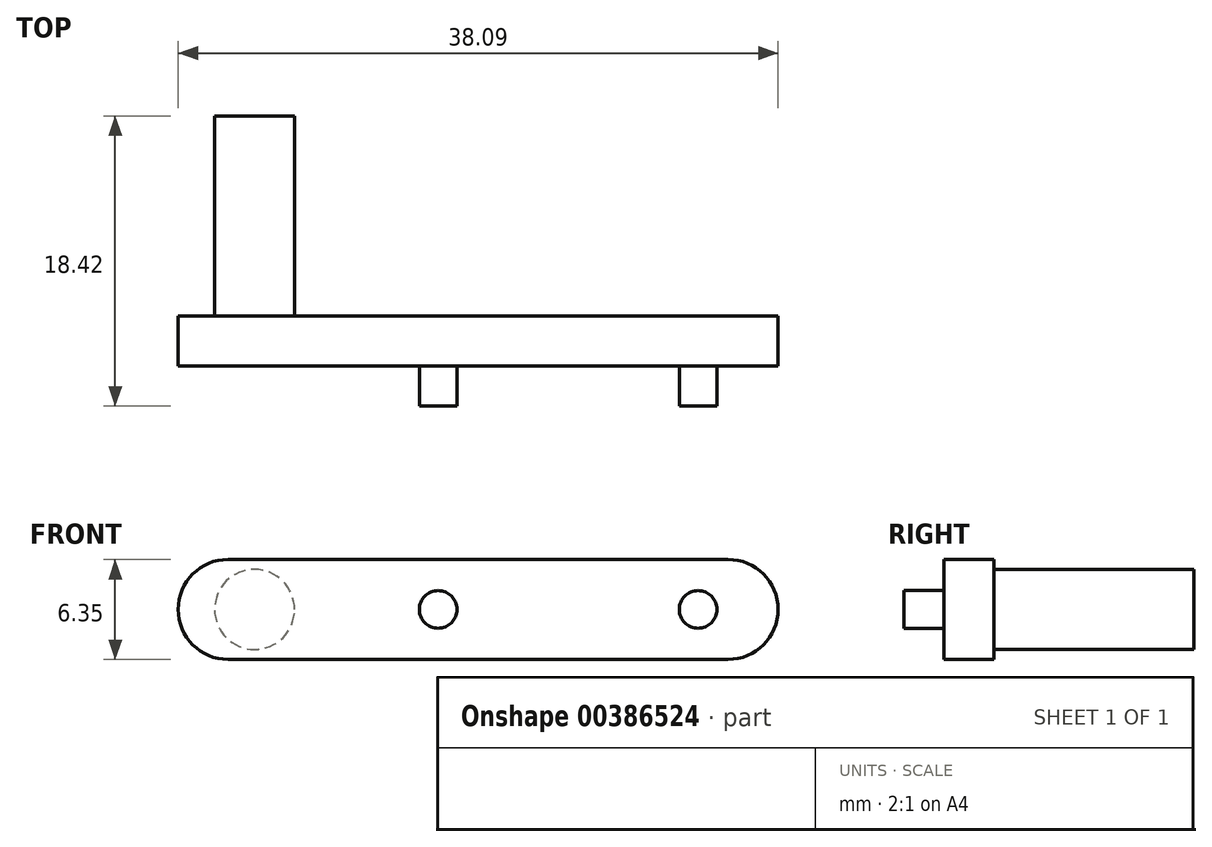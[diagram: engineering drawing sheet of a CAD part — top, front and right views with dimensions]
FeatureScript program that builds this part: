
annotation { "Feature Type Name" : "Feature", "Feature Type Description" : "" }
export const myFeature = defineFeature(function(context is Context, id is Id, definition is map)
    precondition{}
    {
        {
            var Q0;
            Q0=qCreatedBy(makeId("Front.planeOp"),FACE);
            var sketch = newSketch(context, id + "F0", { "sketchPlane" : qUnion([Q0])});
            skArc(sketch, "E0", {"start": v(0, 3.18) * mm, "mid": v(-3.18, 0) * mm, "end": v(0, -3.18) * mm});
            skArc(sketch, "E1", {"start": v(31.75, -3.18) * mm, "mid": v(34.93, 0) * mm, "end": v(31.75, 3.17) * mm});
            skLineSegment(sketch, "E2", {"start": v(0, 3.18) * mm, "end": v(31.75, 3.18) * mm});
            skLineSegment(sketch, "E3", {"start": v(0, -3.17) * mm, "end": v(31.75, -3.18) * mm});
            skSolve(sketch);
        }
        {
            var Q0;
            Q0 = qSketchRegion(id + "F0", true);
            extrude(context, id + "F1", {"entities" : qUnion([Q0]), "depth" : 3.17 * mm});
        }
        {
            var Q0;
            Q0=makeQuery(id+"F1.opExtrude","CAP_FACE",FACE,{"disambiguationData":[OSD([sQuery(id+"F0.wireOp",EDGE,"E0"),sQuery(id+"F0.wireOp",EDGE,"E1"),sQuery(id+"F0.wireOp",EDGE,"E2"),sQuery(id+"F0.wireOp",EDGE,"E3")])],"isStart":false});
            var sketch = newSketch(context, id + "F2", { "sketchPlane" : qUnion([Q0])});
            skCircle(sketch, "E4", {"center": v(13.34, 0) * mm, "radius": 1.2 * mm});
            skSolve(sketch);
        }
        {
            var Q0;
            Q0 = qSketchRegion(id + "F2", true);
            extrude(context, id + "F3", {"entities" : qUnion([Q0]), "operationType" : NewBodyOperationType.ADD, "depth" : 2.54 * mm});
        }
        {
            var Q0;
            Q0=makeQuery(id+"F1.opExtrude","CAP_FACE",FACE,{"disambiguationData":[OSD([sQuery(id+"F0.wireOp",EDGE,"E0"),sQuery(id+"F0.wireOp",EDGE,"E1"),sQuery(id+"F0.wireOp",EDGE,"E2"),sQuery(id+"F0.wireOp",EDGE,"E3")])],"isStart":false});
            var sketch = newSketch(context, id + "F4", { "sketchPlane" : qUnion([Q0])});
            skCircle(sketch, "E5", {"center": v(29.85, 0) * mm, "radius": 1.2 * mm});
            skSolve(sketch);
        }
        {
            var Q0;
            Q0 = qSketchRegion(id + "F4", true);
            extrude(context, id + "F5", {"entities" : qUnion([Q0]), "operationType" : NewBodyOperationType.ADD, "depth" : 2.54 * mm});
        }
        {
            var Q0;
            Q0=makeQuery(id+"F1.opExtrude","CAP_FACE",FACE,{"disambiguationData":[OSD([sQuery(id+"F0.wireOp",EDGE,"E0"),sQuery(id+"F0.wireOp",EDGE,"E1"),sQuery(id+"F0.wireOp",EDGE,"E2"),sQuery(id+"F0.wireOp",EDGE,"E3")])],"isStart":true});
            var sketch = newSketch(context, id + "F6", { "sketchPlane" : qUnion([Q0])});
            skCircle(sketch, "E6", {"center": v(-1.68, 0) * mm, "radius": 2.54 * mm});
            skSolve(sketch);
        }
        {
            var Q0;
            Q0 = qSketchRegion(id + "F6", true);
            extrude(context, id + "F7", {"entities" : qUnion([Q0]), "operationType" : NewBodyOperationType.ADD, "depth" : 12.7 * mm});
        }
    });
